# Revit family: Kessel 97714 en
name_source: partatom
category: Plumbing Fixtures
revit_build: Autodesk Revit Architecture 2014 (Build: 20130308_1515(x64)
units: mm (PartAtom-declared; Revit-internal decimal feet)

## types (1)
- Kessel 97714 en
    <1.010.00.2> Number of the part of the guideline = 4
    <1.010.00.3> Issue date (month) of the guideline = 201410
    <1.010.00.4> Manufacturer name = Kessel
    <1.010.00.5> Revision date of the file = 20190228
    <1.800.00.3> BS number = 10000100000000000000000000000000000000000000000033000
    <1.800.00.4> Comment field = Outdoor control cabinet, H/W/D=1740/590/320 mm
    <1.810.00.3> Manufacturer’s reference number = 97714
    <1.810.00.4> DATANORM number = 97714
    <1.810.00.6> GTIN number = 4026092072905
    <1.960/3L.00.8> Link (URL) = http://www.kessel.de
    <4.100.00.4> Area of application = Accessories
    <4.110.00.4> Model series = Accessories
    <4.700.00.10> Star / delta starting circuit with three-phase connection or three-phase current = no
    <4.700.00.46> vertical installation = no
    <4.700.00.47> outdoor installation = no
    <4.700.00.48> ATEX = no
    <4.700.00.49> protection class = protection class I
    <4.700.00.4> Product name = Outdoor control cabinet, H/W/D=1740/590/320 mm
    <4.700.00.50> motor protection = no
    Manufacturer = Kessel
    Model = 97714
    URL = www.kessel.com
